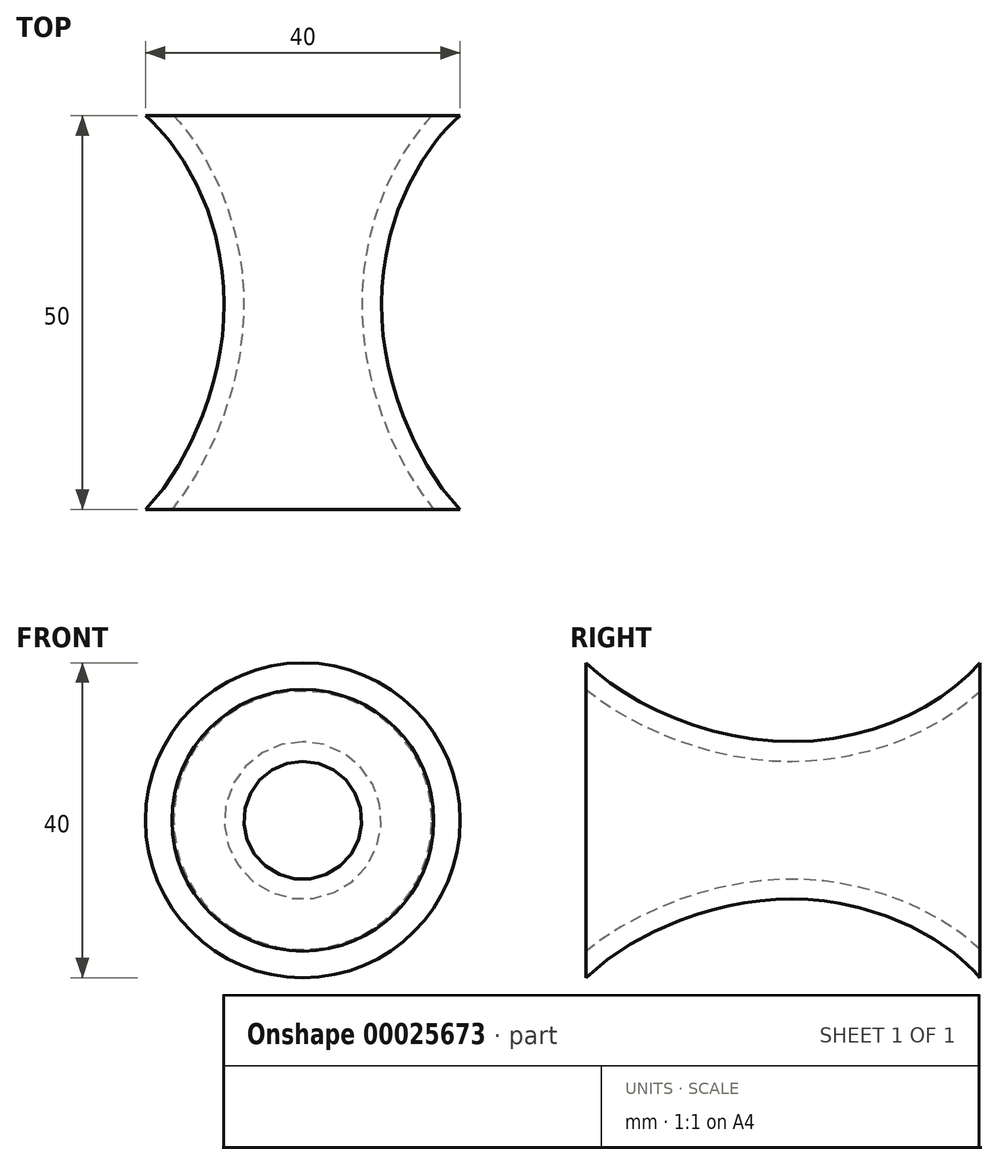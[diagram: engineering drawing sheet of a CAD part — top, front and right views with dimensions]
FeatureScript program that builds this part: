
annotation { "Feature Type Name" : "Feature", "Feature Type Description" : "" }
export const myFeature = defineFeature(function(context is Context, id is Id, definition is map)
    precondition{}
    {
        {
            var Q0;
            Q0=qCreatedBy(makeId("Top.planeOp"),FACE);
            var sketch = newSketch(context, id + "F0", { "sketchPlane" : qUnion([Q0])});
            skFitSpline(sketch, "E0", {"points": [v(20, -25) * mm, v(10, 0) * mm, v(20, 25) * mm], "startDerivative": vector(-30, 30) * mm, "endDerivative": vector(36.85, 31.5) * mm});
            skLineSegment(sketch, "E1", {"start": v(20, 25) * mm, "end": v(0, 25) * mm});
            skLineSegment(sketch, "E2", {"start": v(0, 25) * mm, "end": v(0, -25) * mm});
            skLineSegment(sketch, "E3", {"start": v(0, -25) * mm, "end": v(20, -25) * mm});
            skSolve(sketch);
        }
        {
            var Q0;
            Q0=makeQuery(id+"F0.imprint","IMPRINT",FACE,{"disambiguationData":[TD([[makeQuery(id+"F0.imprint","IMPRINT",EDGE,{"derivedFrom":sQuery(id+"F0.wireOp",EDGE,"E0")}),1.0]])]});
            var Q1;
            Q1=sQuery(id+"F0.wireOp",EDGE,"E2");
            revolve(context, id + "F1", {"entities" : qUnion([Q0]), "axis" : qUnion([Q1]), "revolveType" : RevolveType.FULL});
        }
        {
            var Q0;
            Q0=makeQuery(id+"F1.opRevolve","SWEPT_FACE",FACE,{"disambiguationData":[OSD([sQuery(id+"F0.wireOp",EDGE,"E3")])]});
            var Q1;
            Q1=makeQuery(id+"F1.opRevolve","SWEPT_FACE",FACE,{"disambiguationData":[OSD([sQuery(id+"F0.wireOp",EDGE,"E1")])]});
            shell(context, id + "F2", {"entities" : qUnion([Q0, Q1]), "thickness" : 2.5 * mm});
        }
        {
            var Q0;
            Q0=qCreatedBy(makeId("Top.planeOp"),FACE);
            cPlane(context, id + "F3", {"entities" : qUnion([Q0]), "cplaneType" : CPlaneType.OFFSET, "offset" : 25 * mm, "width" : 150 * mm, "height" : 150 * mm});
        }
    });
